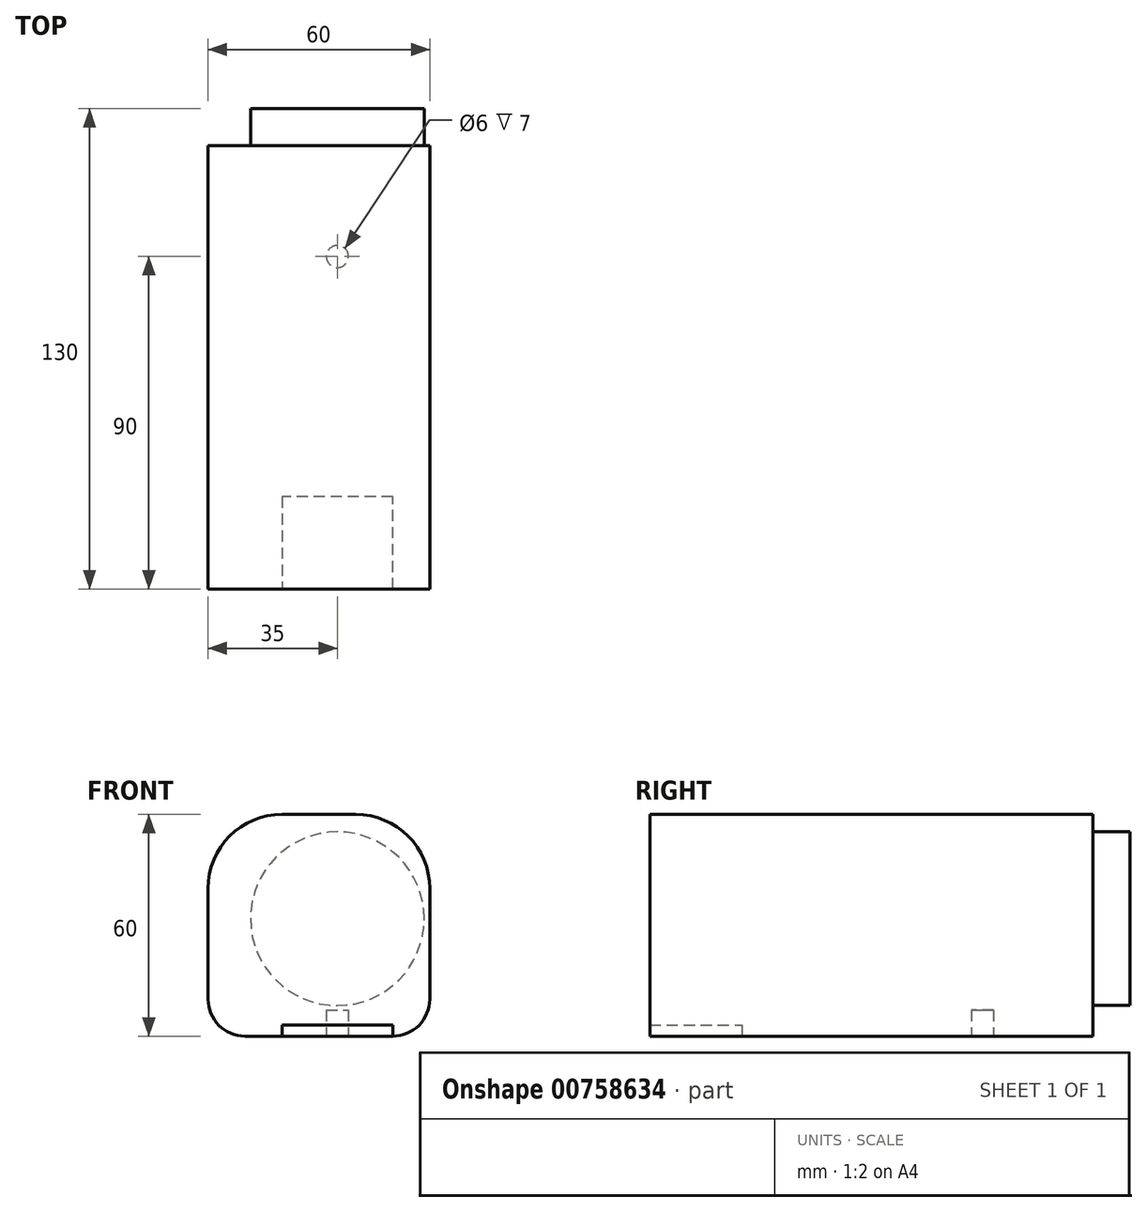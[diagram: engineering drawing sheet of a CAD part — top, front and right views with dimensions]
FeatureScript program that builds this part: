
annotation { "Feature Type Name" : "Feature", "Feature Type Description" : "" }
export const myFeature = defineFeature(function(context is Context, id is Id, definition is map)
    precondition{}
    {
        {
            var Q0;
            Q0=qCreatedBy(makeId("Top.planeOp"),FACE);
            var sketch = newSketch(context, id + "F0", { "sketchPlane" : qUnion([Q0])});
            skLineSegment(sketch, "E0.bottom", {"start": v(30, -60) * mm, "end": v(-30, -60) * mm});
            skLineSegment(sketch, "E0.top", {"start": v(30, 60) * mm, "end": v(-30, 60) * mm});
            skLineSegment(sketch, "E0.left", {"start": v(30, -60) * mm, "end": v(30, 60) * mm});
            skLineSegment(sketch, "E0.right", {"start": v(-30, -60) * mm, "end": v(-30, 60) * mm});
            skPoint(sketch, "E0.middle", {"position": v(0, 0) * mm});
            skSolve(sketch);
        }
        {
            var Q0;
            Q0 = qSketchRegion(id + "F0", true);
            extrude(context, id + "F1", {"entities" : qUnion([Q0]), "depth" : 60 * mm, "offsetDistance" : 25 * mm});
        }
        {
            var Q0;
            Q0=makeQuery(id+"F1.opExtrude","CAP_FACE",FACE,{"disambiguationData":[OSD([sQuery(id+"F0.wireOp",EDGE,"E0.bottom"),sQuery(id+"F0.wireOp",EDGE,"E0.top"),sQuery(id+"F0.wireOp",EDGE,"E0.left"),sQuery(id+"F0.wireOp",EDGE,"E0.right")])],"isStart":true});
            var sketch = newSketch(context, id + "F2", { "sketchPlane" : qUnion([Q0])});
            skCircle(sketch, "E1", {"center": v(5, -30) * mm, "radius": 3 * mm});
            skSolve(sketch);
        }
        {
            var Q0;
            Q0 = qSketchRegion(id + "F2", true);
            extrude(context, id + "F3", {"entities" : qUnion([Q0]), "operationType" : NewBodyOperationType.REMOVE, "oppositeDirection" : true, "depth" : 7 * mm, "offsetDistance" : 25 * mm});
        }
        {
            var Q0;
            Q0=makeQuery(id+"F1.opExtrude","CAP_EDGE",EDGE,{"disambiguationData":[OSD([sQuery(id+"F0.wireOp",EDGE,"E0.left")])],"isStart":false});
            var Q1;
            Q1=makeQuery(id+"F1.opExtrude","CAP_EDGE",EDGE,{"disambiguationData":[OSD([sQuery(id+"F0.wireOp",EDGE,"E0.right")])],"isStart":false});
            fillet(context, id + "F4", {"entities" : qUnion([Q0, Q1]), "radius" : 20 * mm, "tangentPropagation" : true, "allowEdgeOverflow" : false});
        }
        {
            var Q0;
            Q0=makeQuery(id+"F1.opExtrude","CAP_EDGE",EDGE,{"disambiguationData":[OSD([sQuery(id+"F0.wireOp",EDGE,"E0.left")])],"isStart":true});
            var Q1;
            Q1=makeQuery(id+"F1.opExtrude","CAP_EDGE",EDGE,{"disambiguationData":[OSD([sQuery(id+"F0.wireOp",EDGE,"E0.right")])],"isStart":true});
            fillet(context, id + "F5", {"entities" : qUnion([Q0, Q1]), "radius" : 10 * mm, "tangentPropagation" : true, "allowEdgeOverflow" : false});
        }
        {
            var Q0;
            Q0=makeQuery(id+"F1.opExtrude","SWEPT_FACE",FACE,{"disambiguationData":[OSD([sQuery(id+"F0.wireOp",EDGE,"E0.top")])]});
            var sketch = newSketch(context, id + "F6", { "sketchPlane" : qUnion([Q0])});
            skCircle(sketch, "E2", {"center": v(-5, 31.78) * mm, "radius": 23.5 * mm});
            skSolve(sketch);
        }
        {
            var Q0;
            Q0 = qSketchRegion(id + "F6", true);
            extrude(context, id + "F7", {"entities" : qUnion([Q0]), "depth" : 10 * mm, "offsetDistance" : 25 * mm});
        }
        {
            var Q0;
            Q0=makeQuery(id+"F1.opExtrude","CAP_FACE",FACE,{"disambiguationData":[OSD([sQuery(id+"F0.wireOp",EDGE,"E0.bottom"),sQuery(id+"F0.wireOp",EDGE,"E0.top"),sQuery(id+"F0.wireOp",EDGE,"E0.left"),sQuery(id+"F0.wireOp",EDGE,"E0.right")])],"isStart":true});
            var sketch = newSketch(context, id + "F8", { "sketchPlane" : qUnion([Q0])});
            skLineSegment(sketch, "E3.bottom", {"start": v(20, 35) * mm, "end": v(-10, 35) * mm});
            skLineSegment(sketch, "E3.top", {"start": v(20, 60) * mm, "end": v(-10, 60) * mm});
            skLineSegment(sketch, "E3.left", {"start": v(20, 35) * mm, "end": v(20, 60) * mm});
            skLineSegment(sketch, "E3.right", {"start": v(-10, 35) * mm, "end": v(-10, 60) * mm});
            skSolve(sketch);
        }
        {
            var Q0;
            Q0 = qSketchRegion(id + "F8", true);
            extrude(context, id + "F9", {"entities" : qUnion([Q0]), "operationType" : NewBodyOperationType.REMOVE, "oppositeDirection" : true, "depth" : 3 * mm, "offsetDistance" : 25 * mm});
        }
    });
